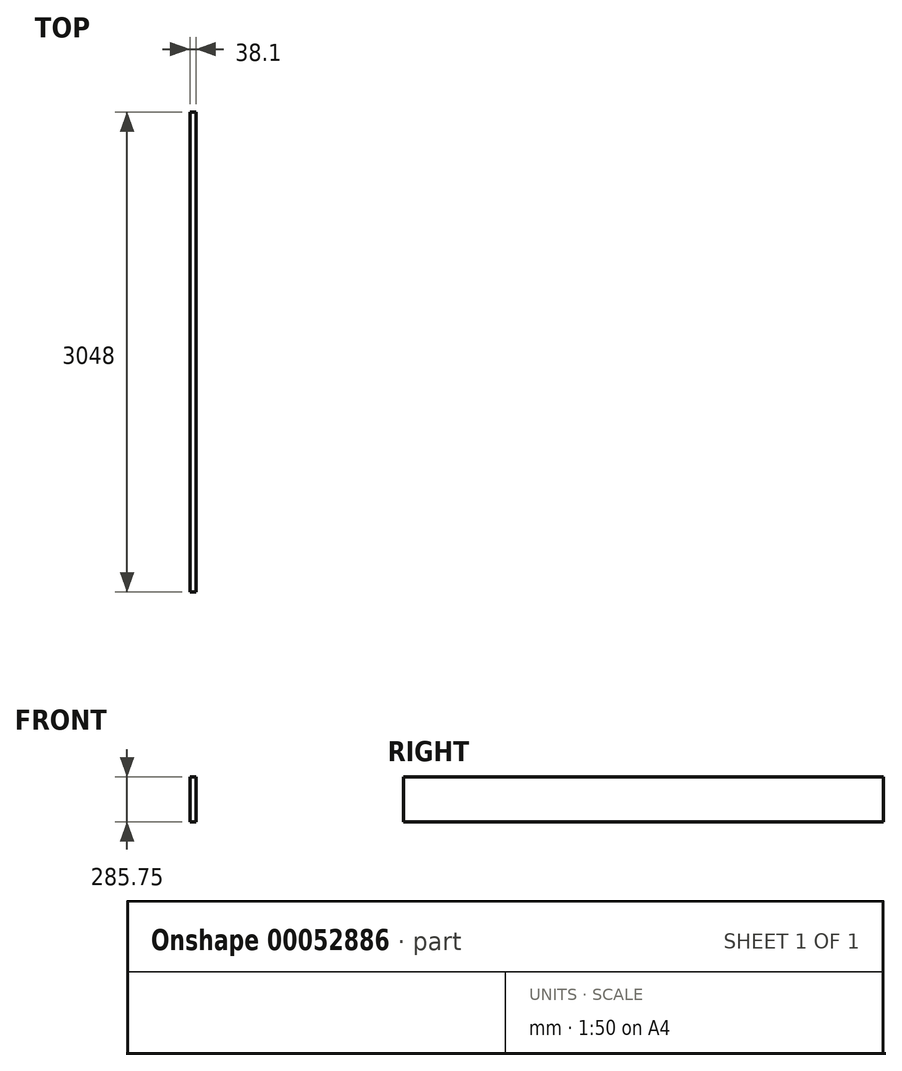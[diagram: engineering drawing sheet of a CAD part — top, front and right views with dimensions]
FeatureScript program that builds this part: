
annotation { "Feature Type Name" : "Feature", "Feature Type Description" : "" }
export const myFeature = defineFeature(function(context is Context, id is Id, definition is map)
    precondition{}
    {
        {
            var Q0;
            Q0=qCreatedBy(makeId("Front.planeOp"),FACE);
            var sketch = newSketch(context, id + "F0", { "sketchPlane" : qUnion([Q0])});
            skLineSegment(sketch, "E0.bottom", {"start": v(0, 0) * mm, "end": v(38.1, 0) * mm});
            skLineSegment(sketch, "E0.top", {"start": v(0, -285.75) * mm, "end": v(38.1, -285.75) * mm});
            skLineSegment(sketch, "E0.left", {"start": v(0, 0) * mm, "end": v(0, -285.75) * mm});
            skLineSegment(sketch, "E0.right", {"start": v(38.1, 0) * mm, "end": v(38.1, -285.75) * mm});
            skSolve(sketch);
        }
        {
            var Q0;
            Q0=qSketchRegion(id+"F0",true);
            extrude(context, id + "F1", {"entities" : qUnion([Q0]), "depth" : 3048 * mm});
        }
    });
